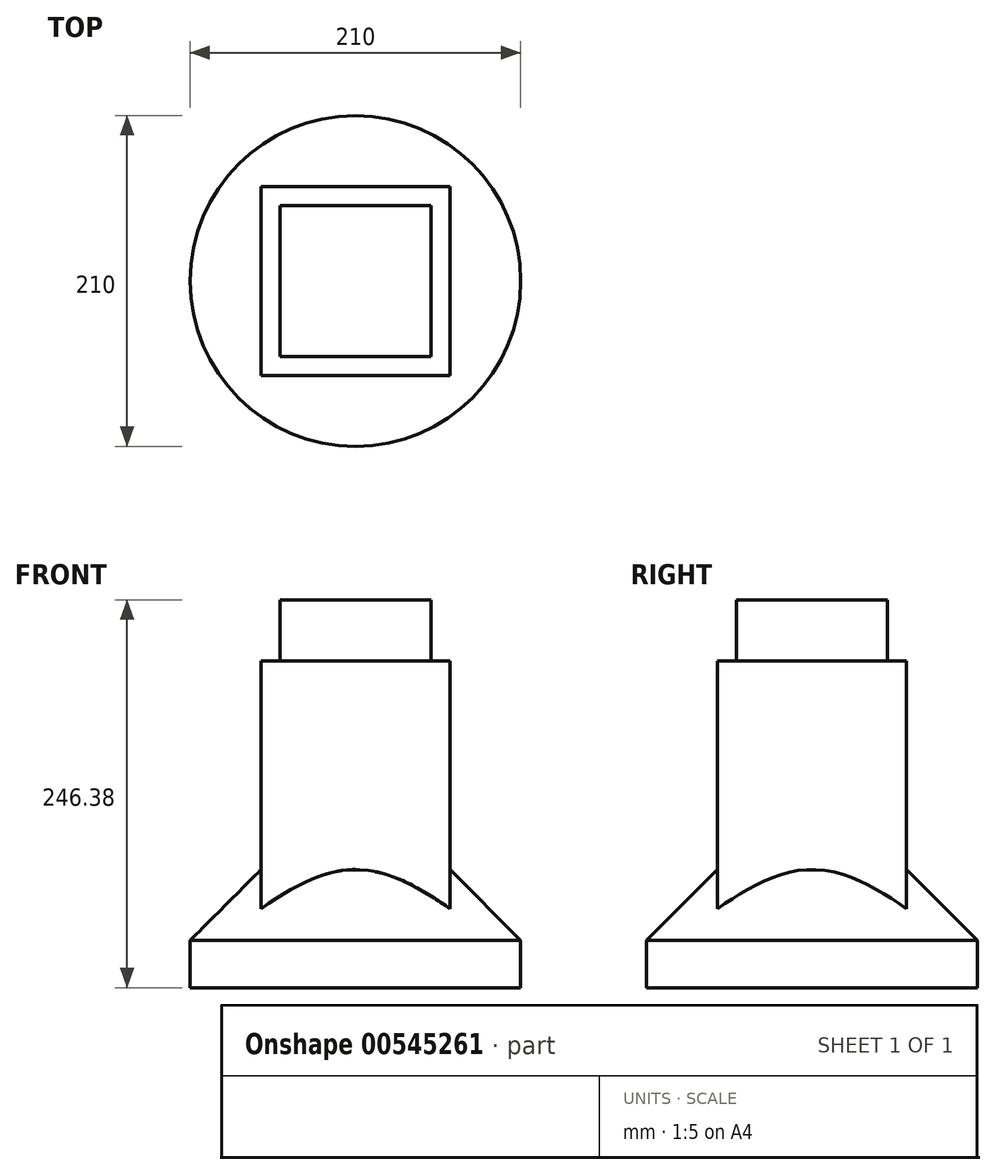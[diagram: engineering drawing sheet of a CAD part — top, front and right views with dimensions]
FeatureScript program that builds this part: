
annotation { "Feature Type Name" : "Feature", "Feature Type Description" : "" }
export const myFeature = defineFeature(function(context is Context, id is Id, definition is map)
    precondition{}
    {
        {
            var Q0;
            Q0=qCreatedBy(makeId("Top.planeOp"),FACE);
            var sketch = newSketch(context, id + "F0", { "sketchPlane" : qUnion([Q0])});
            skLineSegment(sketch, "E0.bottom", {"start": v(0, 0) * mm, "end": v(120, 0) * mm});
            skLineSegment(sketch, "E0.top", {"start": v(0, 120) * mm, "end": v(120, 120) * mm});
            skLineSegment(sketch, "E0.left", {"start": v(0, 0) * mm, "end": v(0, 120) * mm});
            skLineSegment(sketch, "E0.right", {"start": v(120, 0) * mm, "end": v(120, 120) * mm});
            skSolve(sketch);
        }
        {
            var Q0;
            Q0=makeQuery(id+"F0.imprint","IMPRINT",FACE,{"disambiguationData":[TD([[makeQuery(id+"F0.imprint","IMPRINT",EDGE,{"derivedFrom":sQuery(id+"F0.wireOp",EDGE,"E0.bottom")}),1.0]])]});
            extrude(context, id + "F1", {"entities" : qUnion([Q0]), "depth" : 246.38 * mm, "offsetDistance" : 25 * mm});
        }
        {
            var Q0;
            Q0=makeQuery(id+"F1.opExtrude","CAP_FACE",FACE,{"disambiguationData":[OSD([sQuery(id+"F0.wireOp",EDGE,"E0.bottom"),sQuery(id+"F0.wireOp",EDGE,"E0.top"),sQuery(id+"F0.wireOp",EDGE,"E0.left"),sQuery(id+"F0.wireOp",EDGE,"E0.right")])],"isStart":false});
            var sketch = newSketch(context, id + "F2", { "sketchPlane" : qUnion([Q0])});
            skLineSegment(sketch, "E1.bottom", {"start": v(0, 120) * mm, "end": v(120, 120) * mm});
            skLineSegment(sketch, "E1.top", {"start": v(0, 0) * mm, "end": v(120, 0) * mm});
            skLineSegment(sketch, "E1.left", {"start": v(0, 120) * mm, "end": v(0, 0) * mm});
            skLineSegment(sketch, "E1.right", {"start": v(120, 120) * mm, "end": v(120, 0) * mm});
            skLineSegment(sketch, "E2.bottom", {"start": v(12, 108) * mm, "end": v(108, 108) * mm});
            skLineSegment(sketch, "E2.top", {"start": v(12, 12) * mm, "end": v(108, 12) * mm});
            skLineSegment(sketch, "E2.left", {"start": v(12, 108) * mm, "end": v(12, 12) * mm});
            skLineSegment(sketch, "E2.right", {"start": v(108, 108) * mm, "end": v(108, 12) * mm});
            skSolve(sketch);
        }
        {
            var Q0;
            Q0=makeQuery(id+"F2.imprint","IMPRINT",FACE,{"disambiguationData":[TD([[makeQuery(id+"F2.imprint","IMPRINT",EDGE,{"derivedFrom":sQuery(id+"F2.wireOp",EDGE,"E1.bottom")}),-1.0]])]});
            extrude(context, id + "F3", {"entities" : qUnion([Q0]), "operationType" : NewBodyOperationType.REMOVE, "oppositeDirection" : true, "depth" : 39 * mm, "offsetDistance" : 25 * mm});
        }
        {
            var Q0;
            Q0=makeQuery(id+"F1.opExtrude","CAP_FACE",FACE,{"disambiguationData":[OSD([sQuery(id+"F0.wireOp",EDGE,"E0.bottom"),sQuery(id+"F0.wireOp",EDGE,"E0.top"),sQuery(id+"F0.wireOp",EDGE,"E0.left"),sQuery(id+"F0.wireOp",EDGE,"E0.right")])],"isStart":true});
            var sketch = newSketch(context, id + "F4", { "sketchPlane" : qUnion([Q0])});
            skCircle(sketch, "E3", {"center": v(60, -60) * mm, "radius": 105 * mm});
            skLineSegment(sketch, "E4", {"start": v(60, -60) * mm, "end": v(120, -120) * mm, "construction": true});
            skLineSegment(sketch, "E5", {"start": v(120, 0) * mm, "end": v(60, -60) * mm, "construction": true});
            skSolve(sketch);
        }
        {
            var Q0;
            Q0=makeQuery(id+"F4.imprint","IMPRINT",FACE,{"disambiguationData":[TD([[makeQuery(id+"F4.imprint","IMPRINT",EDGE,{"derivedFrom":sQuery(id+"F4.wireOp",EDGE,"E3")}),1.0]])]});
            extrude(context, id + "F5", {"entities" : qUnion([Q0]), "operationType" : NewBodyOperationType.ADD, "oppositeDirection" : true, "depth" : 100 * mm, "offsetDistance" : 25 * mm});
        }
        {
            var Q0;
            Q0=makeQuery(id+"F5.opExtrude","CAP_EDGE",EDGE,{"disambiguationData":[OSD([sQuery(id+"F4.wireOp",EDGE,"E3")])],"isStart":false});
            chamfer(context, id + "F6", {"entities" : qUnion([Q0]), "width" : 70 * mm, "tangentPropagation" : true});
        }
        {
            var Q0;
            Q0=makeQuery(id+"F3.boolean.opBoolean","COPY",FACE,{"derivedFrom":makeQuery(id+"F3.opExtrude","CAP_FACE",FACE,{"disambiguationData":[OSD([sQuery(id+"F2.wireOp",EDGE,"E1.bottom"),sQuery(id+"F2.wireOp",EDGE,"E1.top"),sQuery(id+"F2.wireOp",EDGE,"E1.left"),sQuery(id+"F2.wireOp",EDGE,"E1.right"),sQuery(id+"F2.wireOp",EDGE,"E2.bottom"),sQuery(id+"F2.wireOp",EDGE,"E2.top"),sQuery(id+"F2.wireOp",EDGE,"E2.left"),sQuery(id+"F2.wireOp",EDGE,"E2.right")])],"isStart":false})});
            extrude(context, id + "F7", {"entities" : qUnion([Q0]), "depth" : 80 * mm, "offsetDistance" : 25 * mm});
        }
        {
            var Q0;
            Q0=makeQuery(id+"F7.opExtrude","SWEPT_BODY",BODY,{"disambiguationData":[OSD([sQuery(id+"F2.wireOp",EDGE,"E1.bottom"),sQuery(id+"F2.wireOp",EDGE,"E1.top"),sQuery(id+"F2.wireOp",EDGE,"E1.left"),sQuery(id+"F2.wireOp",EDGE,"E1.right"),sQuery(id+"F2.wireOp",EDGE,"E2.bottom"),sQuery(id+"F2.wireOp",EDGE,"E2.top"),sQuery(id+"F2.wireOp",EDGE,"E2.left"),sQuery(id+"F2.wireOp",EDGE,"E2.right")])]});
            deleteBodies(context, id + "F8", {"entities" : qUnion([Q0])});
        }
    });
